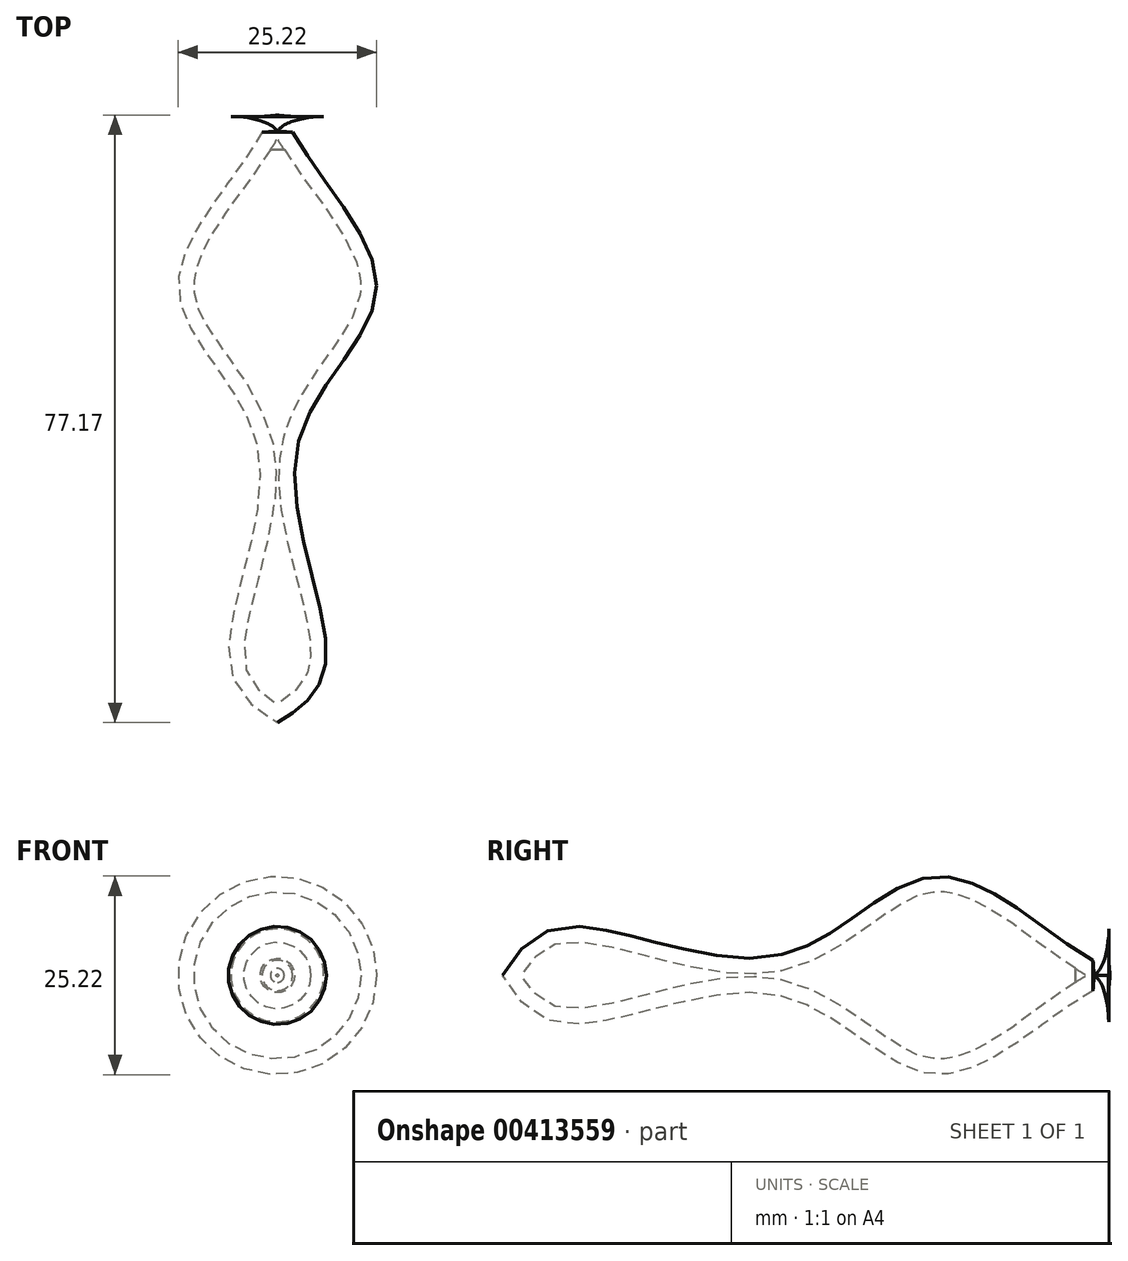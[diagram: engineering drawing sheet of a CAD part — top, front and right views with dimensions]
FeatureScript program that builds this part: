
annotation { "Feature Type Name" : "Feature", "Feature Type Description" : "" }
export const myFeature = defineFeature(function(context is Context, id is Id, definition is map)
    precondition{}
    {
        {
            var Q0;
            Q0=qCreatedBy(makeId("Top.planeOp"),FACE);
            var sketch = newSketch(context, id + "F0", { "sketchPlane" : qUnion([Q0])});
            skLineSegment(sketch, "E0.bottom", {"start": v(40, -75) * mm, "end": v(-40, -75) * mm, "construction": true});
            skLineSegment(sketch, "E0.top", {"start": v(40, 75) * mm, "end": v(-40, 75) * mm, "construction": true});
            skLineSegment(sketch, "E0.left", {"start": v(40, -75) * mm, "end": v(40, 75) * mm, "construction": true});
            skLineSegment(sketch, "E0.right", {"start": v(-40, -75) * mm, "end": v(-40, 75) * mm, "construction": true});
            skPoint(sketch, "E0.middle", {"position": v(0, 0) * mm});
            skLineSegment(sketch, "E1", {"start": v(0, 75) * mm, "end": v(0, 0) * mm, "construction": true});
            skPoint(sketch, "E2.center.orphan", {"position": v(0, 37.5) * mm});
            skArc(sketch, "E3", {"start": v(1.94, 0) * mm, "mid": v(41.6, 38.55) * mm, "end": v(0, 75) * mm});
            skArc(sketch, "E4.0", {"start": v(5.9, 2) * mm, "mid": v(39.5, 40.53) * mm, "end": v(0, 72.99) * mm});
            skFitSpline(sketch, "E5", {"points": [v(1.94, 0) * mm, v(12.6, -19.82) * mm, v(2.5, -40.18) * mm, v(6.14, -67.53) * mm, v(0, -75) * mm], "startDerivative": vector(35.88, -66.28) * mm, "endDerivative": vector(-43.45, -25.58) * mm});
            skFitSpline(sketch, "E6.0", {"points": [v(0.18, -0.95) * mm, v(0.59, -1.71) * mm, v(1.52, -3.23) * mm, v(3.67, -6.3) * mm, v(6, -9.43) * mm, v(8.06, -12.53) * mm, v(9.34, -14.8) * mm, v(10.09, -16.59) * mm, v(10.45, -17.93) * mm, v(10.58, -18.72) * mm, v(10.62, -19.32) * mm, v(10.62, -19.76) * mm, v(10.58, -20.2) * mm, v(10.46, -21.08) * mm, v(10.04, -22.45) * mm, v(9.03, -24.44) * mm, v(7.66, -26.56) * mm, v(6.06, -28.8) * mm, v(4.4, -31.2) * mm, v(3.06, -33.34) * mm, v(2.1, -35.17) * mm, v(1.47, -36.6) * mm, v(0.94, -38.1) * mm, v(0.6, -39.42) * mm, v(0.4, -40.5) * mm, v(0.26, -41.6) * mm, v(0.17, -42.97) * mm, v(0.19, -44.63) * mm, v(0.35, -46.84) * mm, v(0.76, -49.61) * mm, v(1.47, -52.9) * mm, v(2.28, -56.08) * mm, v(3.07, -59.12) * mm, v(3.74, -61.95) * mm, v(4.1, -64.05) * mm, v(4.23, -65.54) * mm, v(4.23, -66.36) * mm, v(4.2, -66.96) * mm, v(4.13, -67.5) * mm, v(3.93, -68.37) * mm, v(3.46, -69.45) * mm, v(2.62, -70.58) * mm, v(1.55, -71.59) * mm, v(0.3, -72.48) * mm, v(-0.58, -73.02) * mm, v(-1.01, -73.28) * mm]});
            skLineSegment(sketch, "E7", {"start": v(0, -72.66) * mm, "end": v(0, -75) * mm});
            skLineSegment(sketch, "E8", {"start": v(0, 75) * mm, "end": v(0, 72.99) * mm});
            skFitSpline(sketch, "E9", {"points": [v(1.43, -3.04) * mm, v(0, 0) * mm, v(5.9, 2) * mm], "startDerivative": vector(-5.1, 8.34) * mm, "endDerivative": vector(14.6, 0) * mm});
            skLineSegment(sketch, "E10", {"start": v(0, -0.65) * mm, "end": v(0, 2) * mm});
            skLineSegment(sketch, "E11", {"start": v(0, 2) * mm, "end": v(5.9, 2) * mm});
            skSolve(sketch);
        }
        {
            var Q0;
            Q0=makeQuery(id+"F0.imprint","IMPRINT",FACE,{"disambiguationData":[TD([[makeQuery(id+"F0.imprint","IMPRINT",EDGE,{"derivedFrom":sQuery(id+"F0.wireOp",EDGE,"E3")}),1.0]])]});
            var Q1;
            Q1=sQuery(id+"F0.wireOp",EDGE,"E10");
            revolve(context, id + "F1", {"entities" : qUnion([Q0]), "axis" : qUnion([Q1]), "revolveType" : RevolveType.FULL});
        }
        {
            var Q0;
            Q0=qCreatedBy(makeId("Top.planeOp"),FACE);
            var sketch = newSketch(context, id + "F2", { "sketchPlane" : qUnion([Q0])});
            skCircle(sketch, "E12", {"center": v(12.02, 13.35) * mm, "radius": 4.14 * mm});
            skCircle(sketch, "E13", {"center": v(7, 23.94) * mm, "radius": 3.24 * mm});
            skCircle(sketch, "E14", {"center": v(26.15, 29.1) * mm, "radius": 6.64 * mm});
            skCircle(sketch, "E15", {"center": v(23.7, 15.66) * mm, "radius": 2.93 * mm});
            skCircle(sketch, "E16", {"center": v(10.94, 44.05) * mm, "radius": 3.71 * mm});
            skCircle(sketch, "E17", {"center": v(10.94, 34.54) * mm, "radius": 4.21 * mm});
            skCircle(sketch, "E18", {"center": v(35.93, 44.86) * mm, "radius": 4.07 * mm});
            skCircle(sketch, "E19", {"center": v(24.11, 46.63) * mm, "radius": 5.1 * mm});
            skCircle(sketch, "E20", {"center": v(15.01, 60.21) * mm, "radius": 5.06 * mm});
            skCircle(sketch, "E21", {"center": v(5.1, 53.15) * mm, "radius": 3.83 * mm});
            skCircle(sketch, "E22", {"center": v(26.97, 59.94) * mm, "radius": 3.29 * mm});
            skCircle(sketch, "E23", {"center": v(8.9, 70.54) * mm, "radius": 2.72 * mm});
            skCircle(sketch, "E24", {"center": v(5.23, 64.02) * mm, "radius": 3.18 * mm});
            skCircle(sketch, "E25", {"center": v(19.22, 69.31) * mm, "radius": 1.81 * mm});
            skCircle(sketch, "E26", {"center": v(22.62, 65.1) * mm, "radius": 2.07 * mm});
            skCircle(sketch, "E27", {"center": v(15.96, 51.52) * mm, "radius": 2.21 * mm});
            skCircle(sketch, "E28", {"center": v(19.9, 38.89) * mm, "radius": 2.21 * mm});
            skCircle(sketch, "E29", {"center": v(32.13, 37.93) * mm, "radius": 1.98 * mm});
            skCircle(sketch, "E30", {"center": v(16.5, 25.57) * mm, "radius": 2.5 * mm});
            skCircle(sketch, "E31", {"center": v(18, 20) * mm, "radius": 1.64 * mm});
            skCircle(sketch, "E32", {"center": v(4.41, 15.8) * mm, "radius": 2.15 * mm});
            skCircle(sketch, "E33", {"center": v(5.5, 8.32) * mm, "radius": 1.85 * mm});
            skCircle(sketch, "E34", {"center": v(11.61, 5.33) * mm, "radius": 1.74 * mm});
            skCircle(sketch, "E35", {"center": v(19.77, 8.19) * mm, "radius": 2.12 * mm});
            skCircle(sketch, "E36", {"center": v(31.72, 20.14) * mm, "radius": 2 * mm});
            skCircle(sketch, "E37", {"center": v(37.97, 30.87) * mm, "radius": 1.82 * mm});
            skCircle(sketch, "E38", {"center": v(37.83, 37.12) * mm, "radius": 1.92 * mm});
            skCircle(sketch, "E39", {"center": v(35.25, 52.2) * mm, "radius": 1.73 * mm});
            skCircle(sketch, "E40", {"center": v(30.36, 54.24) * mm, "radius": 1.96 * mm});
            skCircle(sketch, "E41", {"center": v(22.75, 55.87) * mm, "radius": 1.72 * mm});
            skCircle(sketch, "E42", {"center": v(4.82, 41.2) * mm, "radius": 2.3 * mm});
            skCircle(sketch, "E43", {"center": v(3.2, 46.9) * mm, "radius": 1.73 * mm});
            skCircle(sketch, "E44", {"center": v(3.6, 32.9) * mm, "radius": 2 * mm});
            skCircle(sketch, "E45", {"center": v(2.78, 28.7) * mm, "radius": 0.83 * mm});
            skCircle(sketch, "E46", {"center": v(2.51, 21.5) * mm, "radius": 0.8 * mm});
            skCircle(sketch, "E47", {"center": v(3.2, 3.43) * mm, "radius": 1.36 * mm});
            skCircle(sketch, "E48", {"center": v(3.33, 73.12) * mm, "radius": 1.17 * mm});
            skCircle(sketch, "E49", {"center": v(14.47, 67.82) * mm, "radius": 1.12 * mm});
            skCircle(sketch, "E50", {"center": v(26.42, 38.2) * mm, "radius": 0.98 * mm});
            skCircle(sketch, "E51", {"center": v(4, 58.85) * mm, "radius": 1.42 * mm});
            skCircle(sketch, "E52.MirrorC", {"center": v(-3.33, 73.12) * mm, "radius": 1.17 * mm});
            skCircle(sketch, "E53.MirrorC", {"center": v(-8.9, 70.54) * mm, "radius": 2.72 * mm});
            skCircle(sketch, "E54.MirrorC", {"center": v(-19.22, 69.31) * mm, "radius": 1.81 * mm});
            skCircle(sketch, "E55.MirrorC", {"center": v(-14.47, 67.82) * mm, "radius": 1.12 * mm});
            skCircle(sketch, "E56.MirrorC", {"center": v(-5.23, 64.02) * mm, "radius": 3.18 * mm});
            skCircle(sketch, "E57.MirrorC", {"center": v(-4, 58.85) * mm, "radius": 1.42 * mm});
            skCircle(sketch, "E58.MirrorC", {"center": v(-15.01, 60.21) * mm, "radius": 5.06 * mm});
            skCircle(sketch, "E59.MirrorC", {"center": v(-22.62, 65.1) * mm, "radius": 2.07 * mm});
            skCircle(sketch, "E60.MirrorC", {"center": v(-26.97, 59.94) * mm, "radius": 3.29 * mm});
            skCircle(sketch, "E61.MirrorC", {"center": v(-22.75, 55.87) * mm, "radius": 1.72 * mm});
            skCircle(sketch, "E62.MirrorC", {"center": v(-15.96, 51.52) * mm, "radius": 2.21 * mm});
            skCircle(sketch, "E63.MirrorC", {"center": v(-5.1, 53.15) * mm, "radius": 3.83 * mm});
            skCircle(sketch, "E64.MirrorC", {"center": v(-3.2, 46.9) * mm, "radius": 1.73 * mm});
            skCircle(sketch, "E65.MirrorC", {"center": v(-10.94, 44.05) * mm, "radius": 3.71 * mm});
            skCircle(sketch, "E66.MirrorC", {"center": v(-24.11, 46.63) * mm, "radius": 5.1 * mm});
            skCircle(sketch, "E67.MirrorC", {"center": v(-35.93, 44.86) * mm, "radius": 4.07 * mm});
            skCircle(sketch, "E68.MirrorC", {"center": v(-35.25, 52.2) * mm, "radius": 1.73 * mm});
            skCircle(sketch, "E69.MirrorC", {"center": v(-30.36, 54.24) * mm, "radius": 1.96 * mm});
            skCircle(sketch, "E70.MirrorC", {"center": v(-4.82, 41.2) * mm, "radius": 2.3 * mm});
            skCircle(sketch, "E71.MirrorC", {"center": v(-10.94, 34.54) * mm, "radius": 4.21 * mm});
            skCircle(sketch, "E72.MirrorC", {"center": v(-3.6, 32.9) * mm, "radius": 2 * mm});
            skCircle(sketch, "E73.MirrorC", {"center": v(-2.78, 28.7) * mm, "radius": 0.83 * mm});
            skCircle(sketch, "E74.MirrorC", {"center": v(-2.51, 21.5) * mm, "radius": 0.8 * mm});
            skCircle(sketch, "E75.MirrorC", {"center": v(-4.41, 15.8) * mm, "radius": 2.15 * mm});
            skCircle(sketch, "E76.MirrorC", {"center": v(-5.5, 8.32) * mm, "radius": 1.85 * mm});
            skCircle(sketch, "E77.MirrorC", {"center": v(-3.2, 3.43) * mm, "radius": 1.36 * mm});
            skCircle(sketch, "E78.MirrorC", {"center": v(-11.61, 5.33) * mm, "radius": 1.74 * mm});
            skCircle(sketch, "E79.MirrorC", {"center": v(-19.77, 8.19) * mm, "radius": 2.12 * mm});
            skCircle(sketch, "E80.MirrorC", {"center": v(-23.7, 15.66) * mm, "radius": 2.93 * mm});
            skCircle(sketch, "E81.MirrorC", {"center": v(-31.72, 20.14) * mm, "radius": 2 * mm});
            skCircle(sketch, "E82.MirrorC", {"center": v(-37.97, 30.87) * mm, "radius": 1.82 * mm});
            skCircle(sketch, "E83.MirrorC", {"center": v(-37.83, 37.12) * mm, "radius": 1.92 * mm});
            skCircle(sketch, "E84.MirrorC", {"center": v(-32.13, 37.93) * mm, "radius": 1.98 * mm});
            skCircle(sketch, "E85.MirrorC", {"center": v(-26.15, 29.1) * mm, "radius": 6.64 * mm});
            skCircle(sketch, "E86.MirrorC", {"center": v(-16.5, 25.57) * mm, "radius": 2.5 * mm});
            skCircle(sketch, "E87.MirrorC", {"center": v(-18, 20) * mm, "radius": 1.64 * mm});
            skCircle(sketch, "E88.MirrorC", {"center": v(-26.42, 38.2) * mm, "radius": 0.98 * mm});
            skCircle(sketch, "E89.MirrorC", {"center": v(-19.9, 38.89) * mm, "radius": 2.21 * mm});
            skCircle(sketch, "E90.MirrorC", {"center": v(-12.02, 13.35) * mm, "radius": 4.14 * mm});
            skCircle(sketch, "E91.MirrorC", {"center": v(-7, 23.94) * mm, "radius": 3.24 * mm});
            skSolve(sketch);
        }
        {
            var Q0;
            Q0 = qSketchRegion(id + "F2", true);
            extrude(context, id + "F3", {"entities" : qUnion([Q0]), "operationType" : NewBodyOperationType.REMOVE, "endBound" : BoundingType.SYMMETRIC, "depth" : 90 * mm});
        }
    });
